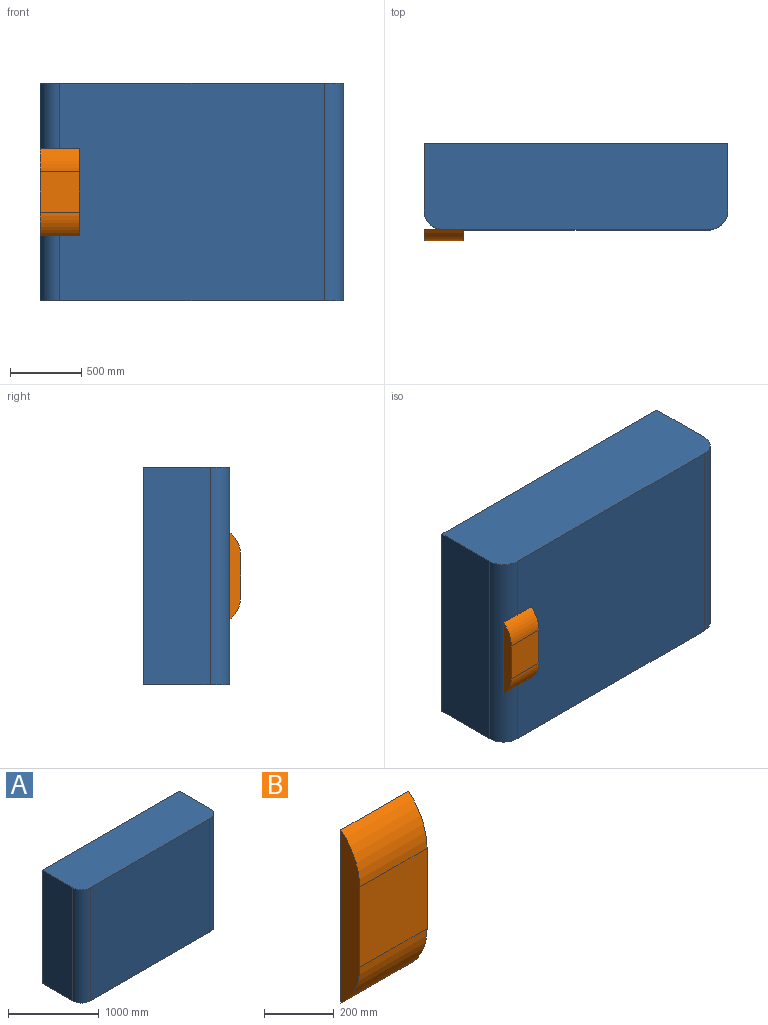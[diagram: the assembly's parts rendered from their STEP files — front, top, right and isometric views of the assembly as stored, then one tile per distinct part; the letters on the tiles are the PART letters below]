
ASSEMBLY  parts=2 mates=1
PART A: 8 faces, bbox 2133.6x609.6x1524 mm
  f0: plane 2133.6x609.6mm, normal (0,0,1), area 1292252.8mm2, adj f1,f3,f4,f5,f6,f7
  f1: plane 1524x469.79mm, normal (-1,0,0), area 715957mm2, adj f0,f2,f5,f6
  f2: plane 2133.6x609.6mm, normal (0,0,-1), area 1292252.8mm2, adj f1,f3,f4,f5,f6,f7
  f3: plane 1524x469.79mm, normal (1,0,0), area 715957mm2, adj f0,f2,f5,f7
  f4: plane 1853.98x1524mm, normal (0,-1,0), area 2825459.6mm2, adj f0,f2,f6,f7
  f5: plane 2133.6x1524mm, normal (0,1,0), area 3251606.4mm2, adj f0,f1,f2,f3
  f6: cylinder r=139.81mm len=1524mm, axis (0,0,1), area 334694.9mm2, adj f0,f1,f2,f4
  f7: cylinder r=139.81mm len=1524mm, axis (0,0,-1), area 334694.9mm2, adj f0,f2,f3,f4
PART B: 6 faces, bbox 274.3x76.2x609.6 mm
  f0: plane 609.6x76.2mm, normal (-1,0,0), area 38849.3mm2, adj f2,f3,f4,f5
  f1: plane 609.6x76.2mm, normal (1,0,0), area 38849.3mm2, adj f2,f3,f4,f5
  f2: plane 282.7x274.32mm, normal (0,-1,0), area 77551.3mm2, adj f0,f1,f4,f5
  f3: plane 609.6x274.32mm, normal (0,1,0), area 167225.5mm2, adj f0,f1,f4,f5
  f4: cylinder r=213.4mm len=274.32mm, axis (1,0,0), area 51074.9mm2, adj f0,f1,f2,f3
  f5: cylinder r=213.4mm len=274.32mm, axis (1,0,0), area 51074.9mm2, adj f0,f1,f2,f3
PLACE A t=(107.79,208,182.53)mm fixed
PLACE B t=(-1806.37,-401.6,490.29)mm
MATE fastened A.f4 <-> B.f3  axis (0,-1,0) through (-1856.89,-401.6,927.44)mm
